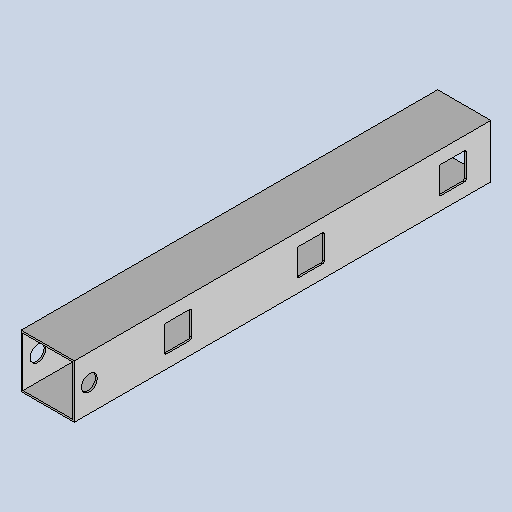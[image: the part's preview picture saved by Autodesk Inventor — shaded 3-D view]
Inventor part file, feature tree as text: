
AUTODESK INVENTOR PART (.ipt)
format: ipt  version: 2025.1 (Build 291241020, 241B)  size: 267,776 bytes
history: native  units: mm
features: sketch x4, projected_geometry x3, extrude x2, fillet x1
ambient origin geometry x8: Origin, YZ Plane, XZ Plane, XY Plane, X Axis, Y Axis, Z Axis, Center Point
bodies: Body1 (feature_tree)
feature tree (10):
  extrude  "Extrusion3"  Depth=60.0mm
  extrude  "Extrusion4"  Depth=2.0mm
  sketch  "Sketch11"  dims[d177=30.5mm]
  sketch  "Sketch13"  dims[d178=30.5mm d179=0.0mm d180=0.0mm d181=47.0mm d182=90.0mm d183=250.0mm d184=400.0mm d185=500.0mm d186=18.0mm d187=2.0mm]
  fillet  "Fillet1"  Radius=470.0mm
  sketch  "Sketch9"  dims[d61=500.0mm d172=60.0mm]
  sketch  "Sketch10"  dims[d173=60.0mm d174=2.0mm d175=470.0mm d176=0.0mm]
  projected_geometry  "Projected Loop3"
  projected_geometry  "Projected Loop4"
  projected_geometry  "Projected Loop5"
